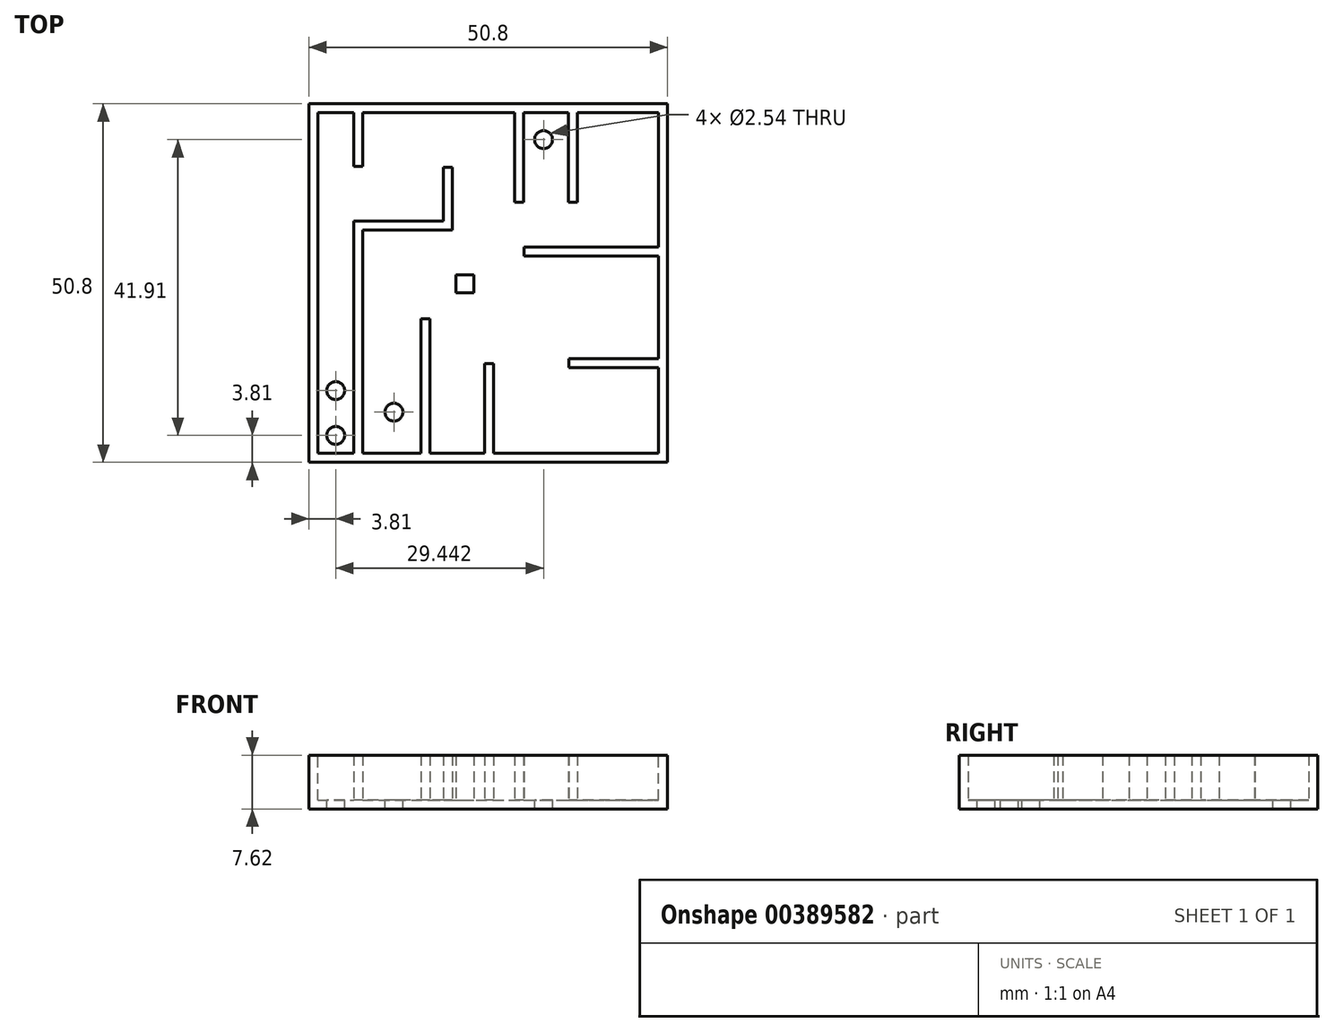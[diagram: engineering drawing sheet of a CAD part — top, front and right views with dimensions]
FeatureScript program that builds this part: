
annotation { "Feature Type Name" : "Feature", "Feature Type Description" : "" }
export const myFeature = defineFeature(function(context is Context, id is Id, definition is map)
    precondition{}
    {
        {
            var Q0;
            Q0=qCreatedBy(makeId("Top.planeOp"),FACE);
            var sketch = newSketch(context, id + "F0", { "sketchPlane" : qUnion([Q0])});
            skLineSegment(sketch, "E0.bottom", {"start": v(0, 0) * mm, "end": v(50.8, 0) * mm});
            skLineSegment(sketch, "E0.top", {"start": v(0, 50.8) * mm, "end": v(50.8, 50.8) * mm});
            skLineSegment(sketch, "E0.left", {"start": v(0, 0) * mm, "end": v(0, 50.8) * mm});
            skLineSegment(sketch, "E0.right", {"start": v(50.8, 0) * mm, "end": v(50.8, 50.8) * mm});
            skSolve(sketch);
        }
        {
            var Q0;
            Q0 = qSketchRegion(id + "F0", true);
            extrude(context, id + "F1", {"entities" : qUnion([Q0]), "oppositeDirection" : true, "depth" : 7.62 * mm});
        }
        {
            var Q0;
            Q0=makeQuery(id+"F1.opExtrude","CAP_FACE",FACE,{"disambiguationData":[OSD([sQuery(id+"F0.wireOp",EDGE,"E0.bottom"),sQuery(id+"F0.wireOp",EDGE,"E0.top"),sQuery(id+"F0.wireOp",EDGE,"E0.left"),sQuery(id+"F0.wireOp",EDGE,"E0.right")])],"isStart":true});
            shell(context, id + "F2", {"entities" : qUnion([Q0]), "thickness" : 1.27 * mm});
        }
        {
            var Q0;
            Q0=makeQuery(id+"F2.opShell","OFFSET_FACE",FACE,{"disambiguationData":[OSD([sQuery(id+"F0.wireOp",EDGE,"E0.bottom"),sQuery(id+"F0.wireOp",EDGE,"E0.top"),sQuery(id+"F0.wireOp",EDGE,"E0.left"),sQuery(id+"F0.wireOp",EDGE,"E0.right")])]});
            var sketch = newSketch(context, id + "F3", { "sketchPlane" : qUnion([Q0])});
            skLineSegment(sketch, "E1", {"start": v(1.27, 1.27) * mm, "end": v(6.35, 1.27) * mm});
            skLineSegment(sketch, "E2", {"start": v(6.35, 1.27) * mm, "end": v(6.35, 32.93) * mm});
            skLineSegment(sketch, "E3", {"start": v(6.35, 32.93) * mm, "end": v(7.62, 32.93) * mm});
            skLineSegment(sketch, "E4", {"start": v(7.62, 32.93) * mm, "end": v(7.62, 1.27) * mm});
            skLineSegment(sketch, "E5", {"start": v(7.62, 1.27) * mm, "end": v(6.35, 1.27) * mm});
            skLineSegment(sketch, "E6", {"start": v(7.62, 49.53) * mm, "end": v(7.62, 41.91) * mm});
            skLineSegment(sketch, "E7", {"start": v(7.62, 41.91) * mm, "end": v(6.35, 41.91) * mm});
            skLineSegment(sketch, "E8", {"start": v(6.35, 41.91) * mm, "end": v(6.35, 49.53) * mm});
            skLineSegment(sketch, "E9", {"start": v(7.62, 49.53) * mm, "end": v(6.35, 49.53) * mm});
            skLineSegment(sketch, "E10", {"start": v(7.62, 32.93) * mm, "end": v(20.32, 32.93) * mm});
            skLineSegment(sketch, "E11", {"start": v(20.32, 32.93) * mm, "end": v(20.32, 41.82) * mm});
            skLineSegment(sketch, "E12", {"start": v(20.32, 41.82) * mm, "end": v(19.05, 41.82) * mm});
            skLineSegment(sketch, "E13", {"start": v(19.05, 41.82) * mm, "end": v(19.05, 34.2) * mm});
            skLineSegment(sketch, "E14", {"start": v(19.05, 34.2) * mm, "end": v(6.35, 34.2) * mm});
            skLineSegment(sketch, "E15", {"start": v(6.35, 34.2) * mm, "end": v(6.35, 32.93) * mm});
            skLineSegment(sketch, "E16", {"start": v(30.43, 49.53) * mm, "end": v(30.43, 36.83) * mm});
            skLineSegment(sketch, "E17", {"start": v(30.43, 36.83) * mm, "end": v(29.16, 36.83) * mm});
            skLineSegment(sketch, "E18", {"start": v(29.16, 36.83) * mm, "end": v(29.16, 49.53) * mm});
            skLineSegment(sketch, "E19", {"start": v(29.16, 49.53) * mm, "end": v(30.43, 49.53) * mm});
            skLineSegment(sketch, "E20", {"start": v(49.53, 30.48) * mm, "end": v(30.48, 30.48) * mm});
            skLineSegment(sketch, "E21", {"start": v(30.48, 30.48) * mm, "end": v(30.48, 29.21) * mm});
            skLineSegment(sketch, "E22", {"start": v(30.48, 29.21) * mm, "end": v(49.53, 29.21) * mm});
            skLineSegment(sketch, "E23", {"start": v(49.53, 30.48) * mm, "end": v(49.53, 29.21) * mm});
            skLineSegment(sketch, "E24", {"start": v(30.43, 49.53) * mm, "end": v(29.16, 49.53) * mm});
            skLineSegment(sketch, "E25", {"start": v(36.78, 49.53) * mm, "end": v(36.78, 36.83) * mm});
            skLineSegment(sketch, "E26", {"start": v(36.78, 36.83) * mm, "end": v(38.05, 36.83) * mm});
            skLineSegment(sketch, "E27", {"start": v(38.05, 36.83) * mm, "end": v(38.05, 49.53) * mm});
            skLineSegment(sketch, "E28", {"start": v(38.05, 49.53) * mm, "end": v(36.78, 49.53) * mm});
            skLineSegment(sketch, "E29", {"start": v(17.13, 1.27) * mm, "end": v(17.13, 20.32) * mm});
            skLineSegment(sketch, "E30", {"start": v(17.13, 20.32) * mm, "end": v(15.86, 20.32) * mm});
            skLineSegment(sketch, "E31", {"start": v(15.86, 20.32) * mm, "end": v(15.86, 1.27) * mm});
            skLineSegment(sketch, "E32", {"start": v(15.86, 1.27) * mm, "end": v(17.13, 1.27) * mm});
            skLineSegment(sketch, "E33", {"start": v(49.53, 13.4) * mm, "end": v(36.83, 13.4) * mm});
            skLineSegment(sketch, "E34", {"start": v(36.83, 13.4) * mm, "end": v(36.83, 14.67) * mm});
            skLineSegment(sketch, "E35", {"start": v(36.83, 14.67) * mm, "end": v(49.53, 14.67) * mm});
            skLineSegment(sketch, "E36", {"start": v(49.53, 14.67) * mm, "end": v(49.53, 13.4) * mm});
            skLineSegment(sketch, "E37", {"start": v(26.15, 1.27) * mm, "end": v(26.15, 13.97) * mm});
            skLineSegment(sketch, "E38", {"start": v(26.15, 13.97) * mm, "end": v(24.88, 13.97) * mm});
            skLineSegment(sketch, "E39", {"start": v(24.88, 13.97) * mm, "end": v(24.88, 1.27) * mm});
            skLineSegment(sketch, "E40", {"start": v(24.88, 1.27) * mm, "end": v(26.15, 1.27) * mm});
            skLineSegment(sketch, "E41", {"start": v(20.86, 26.58) * mm, "end": v(20.86, 24.04) * mm});
            skLineSegment(sketch, "E42", {"start": v(20.86, 26.58) * mm, "end": v(23.4, 26.58) * mm});
            skLineSegment(sketch, "E43", {"start": v(23.4, 26.58) * mm, "end": v(23.4, 24.04) * mm});
            skLineSegment(sketch, "E44", {"start": v(23.4, 24.04) * mm, "end": v(20.86, 24.04) * mm});
            skSolve(sketch);
        }
        {
            var Q0;
            Q0 = qSketchRegion(id + "F3", true);
            extrude(context, id + "F4", {"entities" : qUnion([Q0]), "operationType" : NewBodyOperationType.ADD, "depth" : 6.35 * mm});
        }
        {
            var Q0;
            Q0=makeQuery(id+"F2.opShell","OFFSET_FACE",FACE,{"disambiguationData":[OSD([sQuery(id+"F0.wireOp",EDGE,"E0.bottom"),sQuery(id+"F0.wireOp",EDGE,"E0.top"),sQuery(id+"F0.wireOp",EDGE,"E0.left"),sQuery(id+"F0.wireOp",EDGE,"E0.right")])]});
            var sketch = newSketch(context, id + "F5", { "sketchPlane" : qUnion([Q0])});
            skCircle(sketch, "E45", {"center": v(33.25, 45.72) * mm, "radius": 1.27 * mm});
            skSolve(sketch);
        }
        {
            var Q0;
            Q0=makeQuery(id+"F5.imprint","IMPRINT",FACE,{"disambiguationData":[TD([[makeQuery(id+"F5.imprint","IMPRINT",EDGE,{"derivedFrom":sQuery(id+"F5.wireOp",EDGE,"E45")}),1.0]])]});
            extrude(context, id + "F6", {"entities" : qUnion([Q0]), "operationType" : NewBodyOperationType.REMOVE, "oppositeDirection" : true, "depth" : 25.4 * mm});
        }
        {
            var Q0;
            Q0=makeQuery(id+"F2.opShell","OFFSET_FACE",FACE,{"disambiguationData":[OSD([sQuery(id+"F0.wireOp",EDGE,"E0.bottom"),sQuery(id+"F0.wireOp",EDGE,"E0.top"),sQuery(id+"F0.wireOp",EDGE,"E0.left"),sQuery(id+"F0.wireOp",EDGE,"E0.right")])]});
            var sketch = newSketch(context, id + "F7", { "sketchPlane" : qUnion([Q0])});
            skCircle(sketch, "E46", {"center": v(12.05, 7.1) * mm, "radius": 1.27 * mm});
            skSolve(sketch);
        }
        {
            var Q0;
            Q0=makeQuery(id+"F7.imprint","IMPRINT",FACE,{"disambiguationData":[TD([[makeQuery(id+"F7.imprint","IMPRINT",EDGE,{"derivedFrom":sQuery(id+"F7.wireOp",EDGE,"E46")}),1.0]])]});
            extrude(context, id + "F8", {"entities" : qUnion([Q0]), "operationType" : NewBodyOperationType.REMOVE, "oppositeDirection" : true, "depth" : 25.4 * mm});
        }
        {
            var Q0;
            Q0=makeQuery(id+"F2.opShell","OFFSET_FACE",FACE,{"disambiguationData":[OSD([sQuery(id+"F0.wireOp",EDGE,"E0.bottom"),sQuery(id+"F0.wireOp",EDGE,"E0.top"),sQuery(id+"F0.wireOp",EDGE,"E0.left"),sQuery(id+"F0.wireOp",EDGE,"E0.right")])]});
            var sketch = newSketch(context, id + "F9", { "sketchPlane" : qUnion([Q0])});
            skCircle(sketch, "E47", {"center": v(3.81, 3.81) * mm, "radius": 1.27 * mm});
            skSolve(sketch);
        }
        {
            var Q0;
            Q0 = qSketchRegion(id + "F9", true);
            extrude(context, id + "F10", {"entities" : qUnion([Q0]), "operationType" : NewBodyOperationType.REMOVE, "oppositeDirection" : true, "depth" : 25.4 * mm});
        }
        {
            var Q0;
            Q0=makeQuery(id+"F2.opShell","OFFSET_FACE",FACE,{"disambiguationData":[OSD([sQuery(id+"F0.wireOp",EDGE,"E0.bottom"),sQuery(id+"F0.wireOp",EDGE,"E0.top"),sQuery(id+"F0.wireOp",EDGE,"E0.left"),sQuery(id+"F0.wireOp",EDGE,"E0.right")])]});
            var sketch = newSketch(context, id + "F11", { "sketchPlane" : qUnion([Q0])});
            skCircle(sketch, "E48", {"center": v(3.81, 10.16) * mm, "radius": 1.27 * mm});
            skSolve(sketch);
        }
        {
            var Q0;
            Q0 = qSketchRegion(id + "F11", true);
            extrude(context, id + "F12", {"entities" : qUnion([Q0]), "operationType" : NewBodyOperationType.REMOVE, "oppositeDirection" : true, "depth" : 25.4 * mm});
        }
    });
